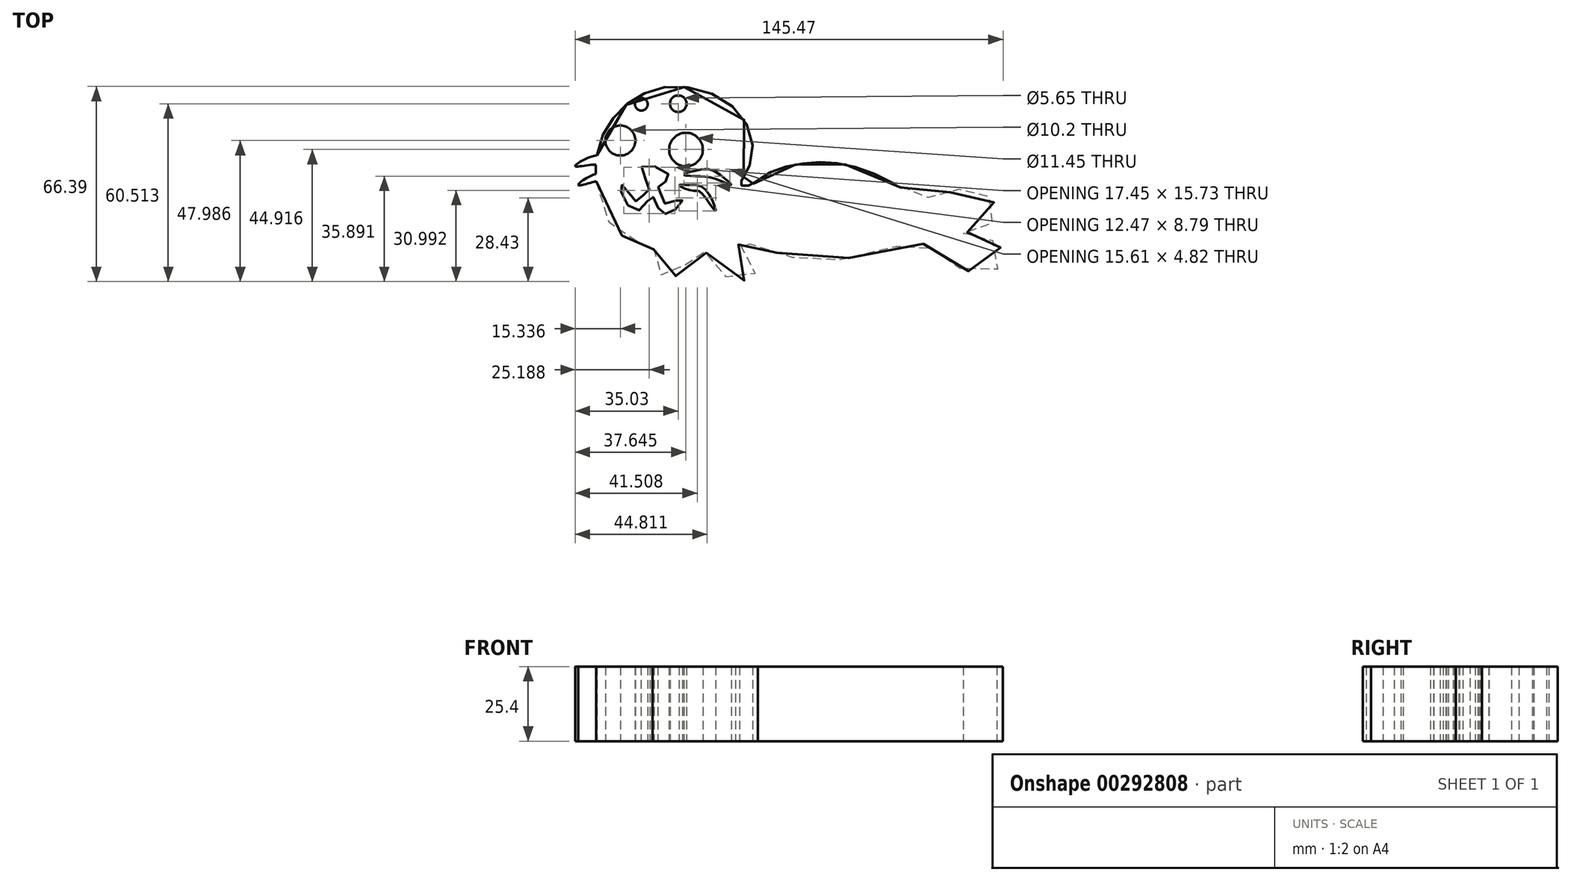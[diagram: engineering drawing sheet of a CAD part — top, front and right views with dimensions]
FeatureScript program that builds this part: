
annotation { "Feature Type Name" : "Feature", "Feature Type Description" : "" }
export const myFeature = defineFeature(function(context is Context, id is Id, definition is map)
    precondition{}
    {
        {
            var Q0;
            Q0=qCreatedBy(makeId("Top.planeOp"),FACE);
            var sketch = newSketch(context, id + "F0", { "sketchPlane" : qUnion([Q0])});
            skFitSpline(sketch, "E0", {"points": [v(-13.45, 8.3) * mm, v(-9.77, 16.09) * mm, v(-14.34, 33.64) * mm, v(-36.44, 41.9) * mm, v(-52.89, 35) * mm, v(-61.54, 20.72) * mm, v(-59.78, -0.94) * mm, v(-49.6, -10.48) * mm, v(-42.88, -11.58) * mm, v(-42.87, -18.5) * mm, v(-36.15, -23.07) * mm, v(-28.58, -14.2) * mm, v(-23.82, -15.72) * mm, v(-14.93, -24.4) * mm, v(-7.35, -18.78) * mm, v(-14.94, -10.98) * mm, v(-5.2, -13.16) * mm, v(18.2, -17.31) * mm, v(48.3, -11.52) * mm, v(56.32, -17.16) * mm, v(73.64, -20.66) * mm, v(74.07, -11.56) * mm, v(62.59, -8.08) * mm, v(72.11, -4.84) * mm, v(72.54, 3.17) * mm, v(62.35, 7.08) * mm, v(51.1, 4.07) * mm, v(35.71, 10.6) * mm, v(19.9, 15.82) * mm, v(7.77, 15.62) * mm, v(-3.7, 12.4) * mm, v(-9.98, 8.3) * mm, v(-11.93, 8.3) * mm, v(-13.45, 8.3) * mm]});
            skCircle(sketch, "E1", {"center": v(-31.74, 20.46) * mm, "radius": 5.72 * mm});
            skCircle(sketch, "E2", {"center": v(-54.05, 23.53) * mm, "radius": 5.1 * mm});
            skFitSpline(sketch, "E3", {"points": [v(-41.26, 7.7) * mm, v(-38.01, 10.07) * mm, v(-38.45, 12.89) * mm, v(-46.9, 14.42) * mm, v(-44.08, 7.7) * mm, v(-45.46, 5.87) * mm, v(-48.46, 2.86) * mm, v(-51.46, 6.28) * mm, v(-53.82, 8.37) * mm, v(-52.3, 2.52) * mm, v(-46.88, 0.12) * mm, v(-43.42, 4.67) * mm, v(-41.25, 0.76) * mm, v(-38.44, -1.4) * mm, v(-33.67, 1.83) * mm, v(-33.19, 3.76) * mm, v(-38.5, 1.9) * mm, v(-40.54, 6) * mm, v(-41.26, 7.7) * mm]});
            skCircle(sketch, "E4", {"center": v(-34.36, 36.05) * mm, "radius": 2.82 * mm});
            skCircle(sketch, "E5", {"center": v(-46.92, 35.86) * mm, "radius": 2.17 * mm});
            skFitSpline(sketch, "E6", {"points": [v(-32.39, 12.01) * mm, v(-28.2, 13.34) * mm, v(-23.74, 13.74) * mm, v(-19.17, 11.12) * mm, v(-16.36, 8.37) * mm, v(-22.42, 10.7) * mm, v(-28.7, 11.35) * mm, v(-32.39, 12.01) * mm]});
            skFitSpline(sketch, "E7", {"points": [v(-34.12, 8.37) * mm, v(-29.35, 6.37) * mm, v(-26.75, 6) * mm, v(-21.7, -0.48) * mm, v(-25.23, 6.97) * mm, v(-31.08, 8.37) * mm, v(-34.12, 8.37) * mm]});
            skFitSpline(sketch, "E8", {"points": [v(-50.8, 14) * mm, v(-53.82, 16.16) * mm, v(-62.6, 18.35) * mm, v(-69.37, 14.83) * mm, v(-62.34, 15.35) * mm, v(-58.68, 14.7) * mm, v(-56.51, 14.7) * mm, v(-50.8, 14) * mm]});
            skFitSpline(sketch, "E9", {"points": [v(-53.82, 10.75) * mm, v(-60.1, 12.7) * mm, v(-68.33, 8.37) * mm, v(-62.33, 9.68) * mm, v(-56.51, 10.22) * mm, v(-53.82, 10.75) * mm]});
            skSolve(sketch);
        }
        {
            var Q0;
            Q0 = qSketchRegion(id + "F0", true);
            extrude(context, id + "F1", {"entities" : qUnion([Q0]), "depth" : 25.4 * mm});
        }
    });
